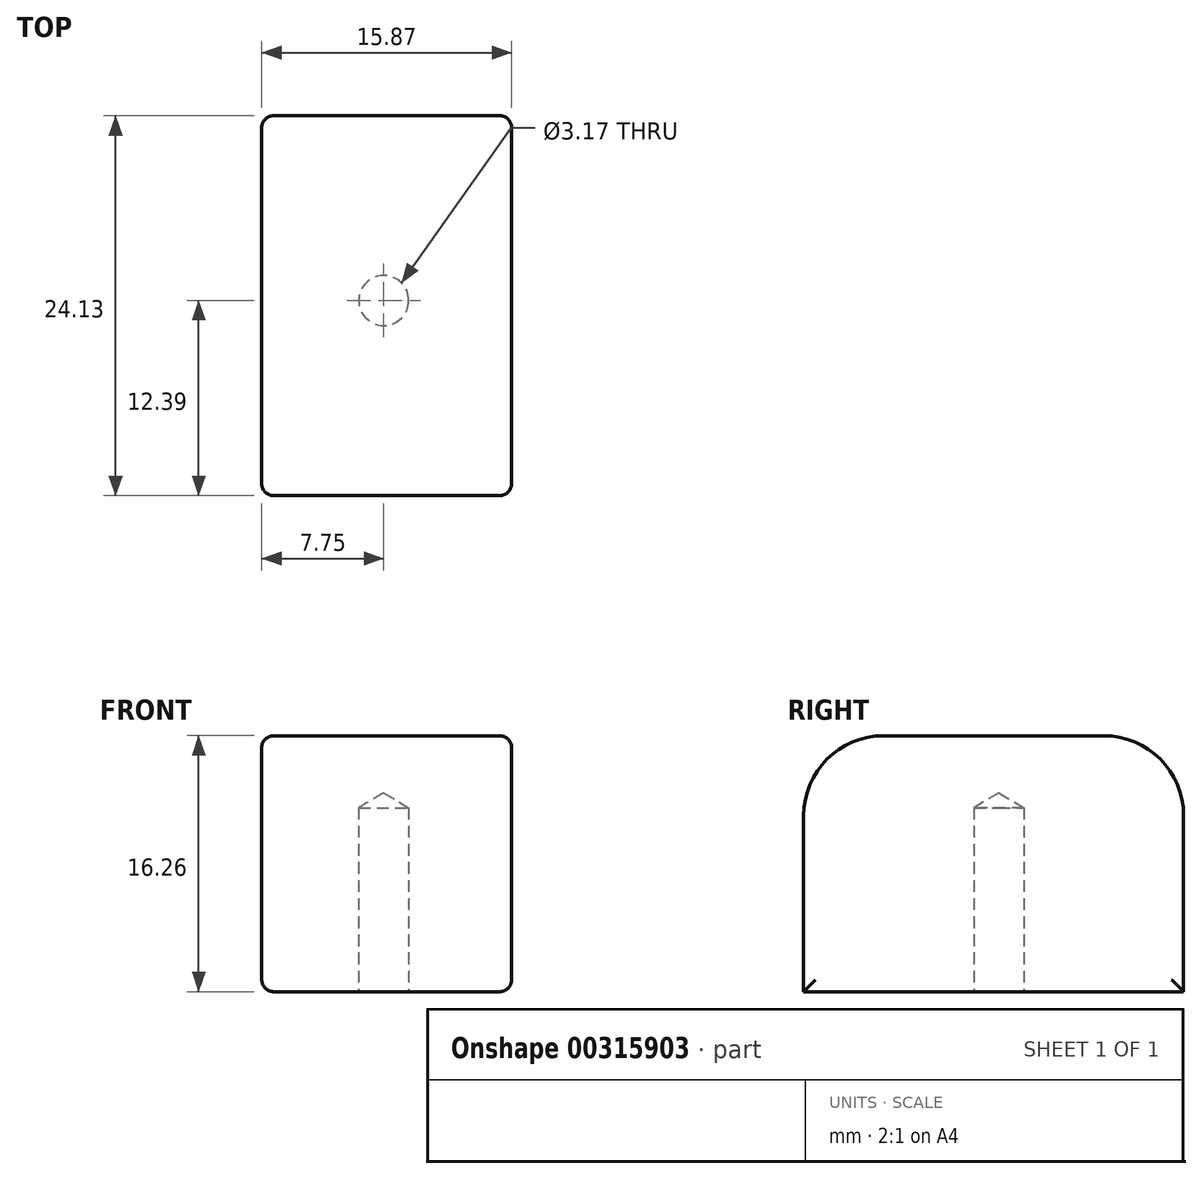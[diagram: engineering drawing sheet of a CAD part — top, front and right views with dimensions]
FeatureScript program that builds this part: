
annotation { "Feature Type Name" : "Feature", "Feature Type Description" : "" }
export const myFeature = defineFeature(function(context is Context, id is Id, definition is map)
    precondition{}
    {
        {
            var Q0;
            Q0=qCreatedBy(makeId("Top.planeOp"),FACE);
            var sketch = newSketch(context, id + "F0", { "sketchPlane" : qUnion([Q0])});
            skLineSegment(sketch, "E0.bottom", {"start": v(-7.75, 11.74) * mm, "end": v(8.12, 11.74) * mm});
            skLineSegment(sketch, "E0.top", {"start": v(-7.75, -12.39) * mm, "end": v(8.12, -12.39) * mm});
            skLineSegment(sketch, "E0.left", {"start": v(-7.75, 11.74) * mm, "end": v(-7.75, -12.39) * mm});
            skLineSegment(sketch, "E0.right", {"start": v(8.12, 11.74) * mm, "end": v(8.12, -12.39) * mm});
            skLineSegment(sketch, "E1", {"start": v(0, 29.83) * mm, "end": v(0, -26.58) * mm, "construction": true});
            skLineSegment(sketch, "E2", {"start": v(-37.14, 0) * mm, "end": v(34.13, 0) * mm, "construction": true});
            skPoint(sketch, "E3", {"position": v(0, 0) * mm});
            skSolve(sketch);
        }
        {
            var Q0;
            Q0=makeQuery(id+"F0.imprint","IMPRINT",FACE,{"disambiguationData":[TD([[makeQuery(id+"F0.imprint","IMPRINT",EDGE,{"derivedFrom":sQuery(id+"F0.wireOp",EDGE,"E0.bottom")}),-1.0]])]});
            extrude(context, id + "F1", {"entities" : qUnion([Q0]), "depth" : 16.26 * mm});
        }
        {
            var Q0;
            Q0=sQuery(id+"F0.wireOp",VERTEX,"E3");
            var Q1;
            Q1=makeQuery(id+"F1.opExtrude","SWEPT_BODY",BODY,{"disambiguationData":[OSD([sQuery(id+"F0.wireOp",EDGE,"E0.bottom"),sQuery(id+"F0.wireOp",EDGE,"E0.top"),sQuery(id+"F0.wireOp",EDGE,"E0.left"),sQuery(id+"F0.wireOp",EDGE,"E0.right")])]});
            hole(context, id + "F2", {"style" : HoleStyle.SIMPLE, "endStyle" : HoleEndStyle.BLIND, "oppositeDirection" : true, "holeDiameter" : 3.17 * mm, "holeDepth" : 11.68 * mm, "tappedDepth" : 12.7 * mm, "tapClearance" : 3, "startFromSketch" : true, "locations" : qUnion([Q0]), "scope" : qUnion([Q1])});
        }
        {
            var Q0;
            Q0=makeQuery(id+"F1.opExtrude","CAP_EDGE",EDGE,{"disambiguationData":[OSD([sQuery(id+"F0.wireOp",EDGE,"E0.top")])],"isStart":false});
            var Q1;
            Q1=makeQuery(id+"F1.opExtrude","CAP_EDGE",EDGE,{"disambiguationData":[OSD([sQuery(id+"F0.wireOp",EDGE,"E0.bottom")])],"isStart":false});
            fillet(context, id + "F3", {"entities" : qUnion([Q0, Q1]), "radius" : 5.08 * mm, "tangentPropagation" : true, "allowEdgeOverflow" : false});
        }
        {
            var Q0;
            Q0=makeQuery(id+"F1.opExtrude","SWEPT_FACE",FACE,{"disambiguationData":[OSD([sQuery(id+"F0.wireOp",EDGE,"E0.right")])]});
            var Q1;
            Q1=makeQuery(id+"F1.opExtrude","SWEPT_FACE",FACE,{"disambiguationData":[OSD([sQuery(id+"F0.wireOp",EDGE,"E0.left")])]});
            fillet(context, id + "F4", {"entities" : qUnion([Q0, Q1]), "radius" : 0.76 * mm, "tangentPropagation" : true, "allowEdgeOverflow" : false});
        }
    });
